# Revit family: Shower-Bath_and_Shower_Trim-KOHLER-Toobi-K-T8975
name_source: partatom
category: Plumbing Fixtures
revit_build: Autodesk Revit 2015 (Build: 20140606_1530(x64)
units: mm (PartAtom-declared; Revit-internal decimal feet)

## types (4) — shared parameters
ADA Compliant = No
Assembly Code = D2010700
CW Connection = No
Cold Water Inlet = Cold Water Inlet
Date Modified = 3/22/2019
Default Elevation = 42"
Drain Included = No
Flow Rate = 2 GPM
HW Connection = Yes
Height = 6 1/2"
Hot Water Inlet = Hot Water Inlet
Manufacturer = KOHLER Co.
MasterFormat 1995 = 15410
MasterFormat 2004 = 22.41.23
Material = Premium Material Construction
Pressure = 80.00 psi
Product Documentation Link = https://www.us.kohler.com
Product Name = Toobi
Product Page URL = http://www.us.kohler.com
Spout Reach = 6 3/4"
Tempered Water Inlet 1 = Tempered Water Inlet 1
Tempered Water Inlet 2 = Tempered Water Inlet 2
URL = https://www.us.kohler.com
Vent Connection = No
Waste Connection = No
Waste Water Outlet = Waste Water Outlet
WaterSense Certified = Yes
Width = 6 1/2"

## per-type parameters (varying)
| type | Description | Finish | Less Showerhead | Model | Showerhead | Type |
| With Showerhead-CP-Polished Chrome | bath and shower trim set, valve not included | Kohler-Metal-CP-Polished_Chrome | No | K-T8975-4-CP | Yes | 1 |
| With Showerhead-BN-Vibrant Brushed Nickel | bath and shower trim set, valve not included | Kohler-Metal-BN-Vibrant_Brushed_Nickel | No | K-T8975-4-BN | Yes | 2 |
| Without Showerhead-CP-Polished Chrome | Rite-Temp bath and shower trim set with push-button diverter, less showerhead | Kohler-Metal-CP-Polished_Chrome | Yes | K-T8975-4L-CP | No | 3 |
| Without Showerhead-BN-Vibrant Brushed Nickel | Rite-Temp bath and shower trim set with push-button diverter, less showerhead | Kohler-Metal-BN-Vibrant_Brushed_Nickel | Yes | K-T8975-4L-BN | No | 4 |

## geometry (parser evidence)
native form markers: Sweep x8
no freeform markers — native parametric forms only
